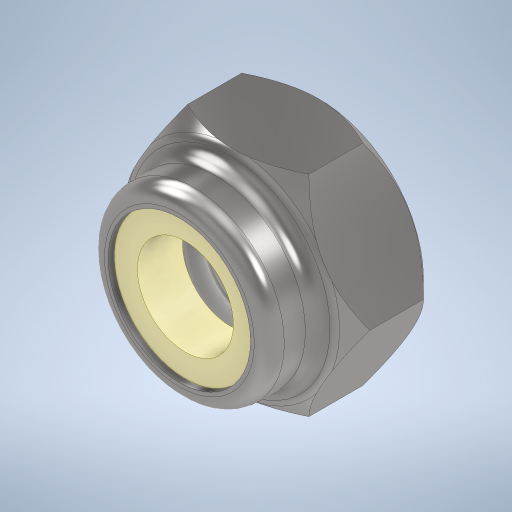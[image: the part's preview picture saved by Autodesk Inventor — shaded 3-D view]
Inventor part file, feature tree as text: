
AUTODESK INVENTOR PART (.ipt)
format: ipt  version: 2024 (Build 280153000, 153)  size: 375,808 bytes
history: native  units: mm
features: sketch x6, extrude x5, chamfer x2, hole x2, fillet x1, projected_geometry x1, other x1
ambient origin geometry x8: Origin, YZ Plane, XZ Plane, XY Plane, X Axis, Y Axis, Z Axis, Center Point
bodies: Solid1 (feature_tree)
feature tree (18):
  sketch  "Sketch1"  dims[d0=7.0mm d2=3.0mm d3=0.0mm d4=0.6mm d5=2.0mm d6=45.0deg]
  extrude  "Extrusion1"  Depth=3.0mm TaperAngle=0.0deg
  chamfer  "Chamfer1"  Distance=0.6mm Angle=45.0deg
  extrude  "Extrusion2"  Depth=6.0mm
  extrude  "Extrusion3"  Depth=0.5mm
  fillet  "Fillet1"  Radius=4.75mm
  extrude  "Extrusion4"  Depth=1.5mm TaperAngle=0.0deg
  extrude  "Extrusion5"  Depth=0.25mm TaperAngle=45.0deg
  hole  "Hole1"  [1 undecoded]
  hole  "Hole2"  [1 undecoded]
  chamfer  "Chamfer2"  [1 undecoded]
  sketch  "Sketch2"  dims[d7=0.0mm d8=0.0mm d9=6.0mm]
  sketch  "Sketch3"  dims[d10=1.7mm d11=0.0mm d12=0.5mm d13=4.75mm]
  sketch  "Sketch4"  dims[d14=1.7mm d15=0.0mm d16=1.5mm d17=0.0mm]
  projected_geometry  "Projected Loop1"
  other  "Lockring"
  sketch  "Sketch5"  dims[d18=3.242mm d19=8.0mm d20=4.0mm d21=2.0mm d22=90.0deg d23=11.8mm d24=0.0mm]
  sketch  "Sketch6"  dims[d25=3.2mm d26=8.0mm d27=4.0mm d28=2.0mm d29=90.0deg d30=8.0mm d31=0.0mm d32=0.25mm d33=2.0mm d34=45.0deg]
note: 3 required parameter values undecoded (feature->parameter linkage not recoverable at this tier; creation-order binding heuristic only, values carry confidence <= 0.55)
